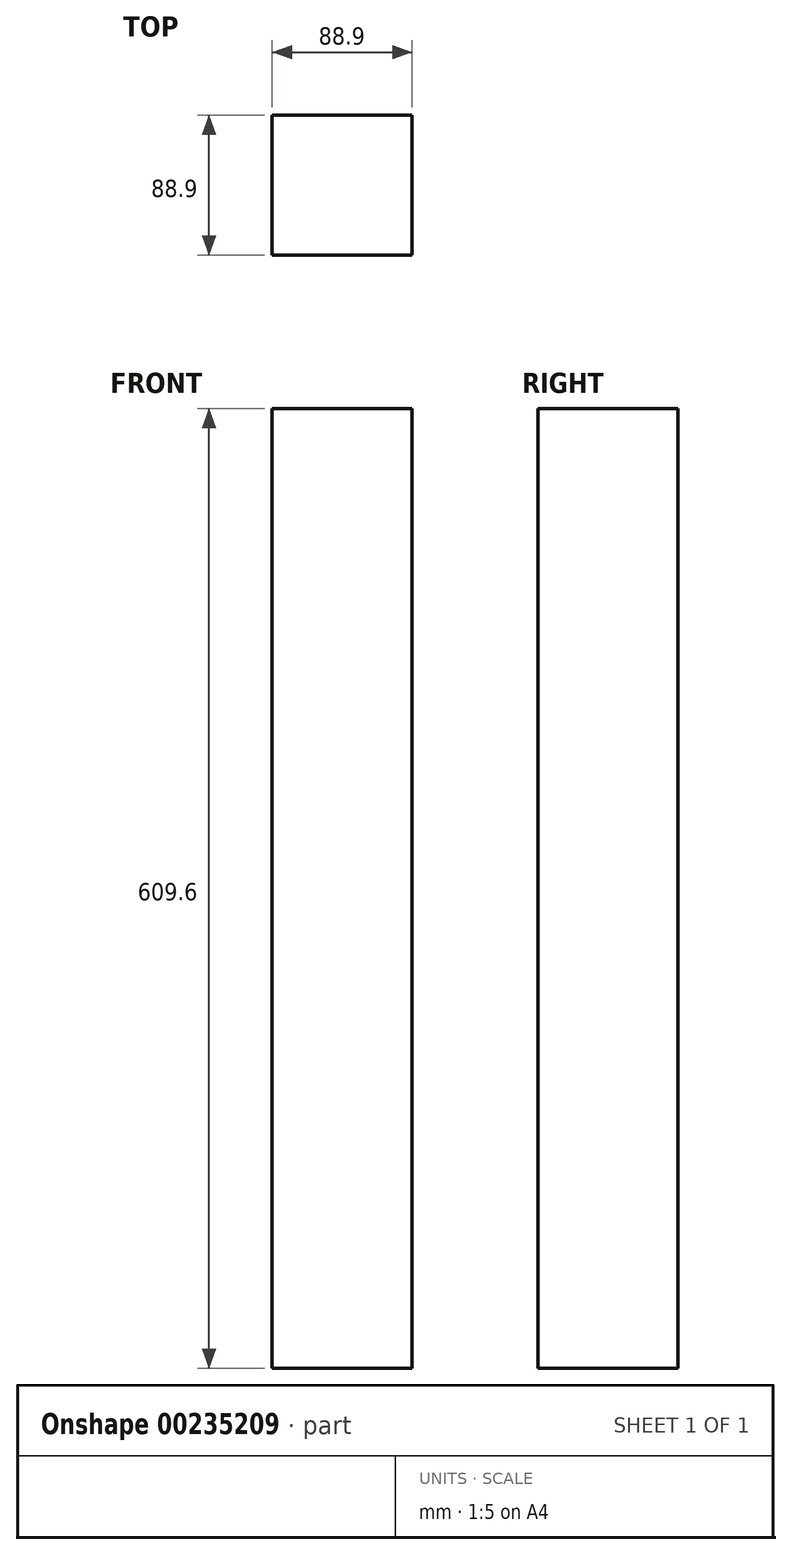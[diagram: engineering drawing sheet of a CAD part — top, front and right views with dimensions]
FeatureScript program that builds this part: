
annotation { "Feature Type Name" : "Feature", "Feature Type Description" : "" }
export const myFeature = defineFeature(function(context is Context, id is Id, definition is map)
    precondition{}
    {
        {
            var Q0;
            Q0=qCreatedBy(makeId("Top.planeOp"),FACE);
            var sketch = newSketch(context, id + "F0", { "sketchPlane" : qUnion([Q0])});
            skLineSegment(sketch, "E0.bottom", {"start": v(44.45, 44.45) * mm, "end": v(-44.45, 44.45) * mm});
            skLineSegment(sketch, "E0.top", {"start": v(44.45, -44.45) * mm, "end": v(-44.45, -44.45) * mm});
            skLineSegment(sketch, "E0.left", {"start": v(44.45, 44.45) * mm, "end": v(44.45, -44.45) * mm});
            skLineSegment(sketch, "E0.right", {"start": v(-44.45, 44.45) * mm, "end": v(-44.45, -44.45) * mm});
            skPoint(sketch, "E0.middle", {"position": v(0, 0) * mm});
            skSolve(sketch);
        }
        {
            var Q0;
            Q0=makeQuery(id+"F0.imprint","IMPRINT",FACE,{"disambiguationData":[TD([[makeQuery(id+"F0.imprint","IMPRINT",EDGE,{"derivedFrom":sQuery(id+"F0.wireOp",EDGE,"E0.bottom")}),1.0]])]});
            extrude(context, id + "F1", {"entities" : qUnion([Q0]), "depth" : 609.6 * mm});
        }
    });
